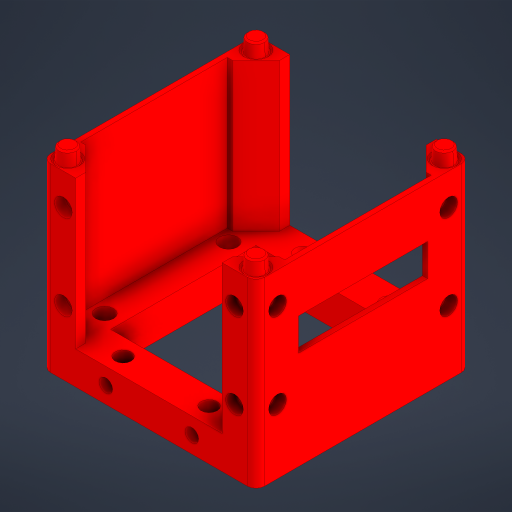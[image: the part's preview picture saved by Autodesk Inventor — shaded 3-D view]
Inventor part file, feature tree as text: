
AUTODESK INVENTOR PART (.ipt)
format: ipt  version: 2023.3 (Build 273359000, 359)  size: 446,976 bytes
history: native  units: mm
features: extrude x9, chamfer x7, sketch x5, projected_geometry x2, pattern_linear x1, pattern_circular x1, fillet x1
ambient origin geometry x8: Origin, YZ Plane, XZ Plane, XY Plane, X Axis, Y Axis, Z Axis, Center Point
bodies: Solid1 (feature_tree)
feature tree (26):
  sketch  "Sketch1"  dims[d0=49.8mm d1=49.8mm]
  extrude  "Extrusion1"  Depth=49.8mm
  extrude  "Extrusion2"  Depth=8.0mm
  extrude  "Extrusion3"  Depth=4.1mm
  extrude  "Extrusion4"  Depth=3.0mm
  chamfer  "Chamfer1"  Distance=4.2625mm
  chamfer  "Chamfer2"  Distance=0.675mm
  chamfer  "Chamfer3"  Distance=7.85mm
  chamfer  "Chamfer4"  Distance=7.85mm
  chamfer  "Chamfer5"  Distance=5.5mm
  chamfer  "Chamfer6"  Distance=5.5mm
  sketch  "Sketch2"  dims[d2=8.0mm d3=10.5mm]
  extrude  "Extrusion5"  Depth=10.0mm TaperAngle=360.0deg
  extrude  "Extrusion6"  Depth=7.7mm TaperAngle=0.0deg
  pattern_linear  "Rectangular Pattern1"  Spacing1=34.4mm  [1 undecoded]
  pattern_circular  "Circular Pattern1"  [2 undecoded]
  extrude  "Extrusion7"  Depth=10.0mm TaperAngle=0.0deg
  fillet  "Fillet1"  Radius=2.0mm
  chamfer  "Chamfer7"  Distance=0.375mm Angle=45.0deg
  extrude  "Extrusion8"  Depth=2.0mm
  extrude  "Extrusion9"  Depth=2.0mm
  sketch  "Sketch3"  dims[d4=10.5mm d5=4.1mm]
  projected_geometry  "Projected Loop1"
  sketch  "Sketch4"  dims[d6=4.15mm d7=3.0mm]
  projected_geometry  "Projected Loop2"
  sketch  "Sketch5"  dims[d8=3.0mm d9=4.2625mm d10=0.675mm d11=7.85mm d12=7.85mm d13=5.5mm d14=5.5mm d15=40.0mm d17=360.0deg d19=7.7mm d20=0.0mm d21=34.4mm d22=0.0mm d23=0.375mm d24=0.0mm d25=3.25mm d26=0.0mm d27=0.5mm d28=2.0mm d29=45.0deg d30=0.375mm d31=2.0mm d32=45.0deg d33=2.75mm d34=2.0mm d35=0.436332mm d36=2.75mm d37=2.0mm d38=0.436332mm d39=2.75mm d40=2.0mm d41=0.436332mm d42=2.75mm d43=2.0mm d44=0.436332mm d45=10.0mm d46=3.125mm d47=5.0mm d48=15.0mm d49=4.125mm d50=3.25mm d51=0.0mm d52=2.5mm d53=0.0mm d54=20.0mm d56=19.8mm d57=40.0mm d58=360.0deg d60=3.75mm d61=5.0mm d62=5.0mm d63=5.4125mm d64=0.0mm d65=2.0mm d66=0.025mm d67=2.0mm d68=0.436332mm d69=10.0mm d70=0.0mm d71=26.625mm d72=30.0mm d73=7.5mm d74=10.0mm d75=0.0mm]
note: 3 required parameter values undecoded (feature->parameter linkage not recoverable at this tier; creation-order binding heuristic only, values carry confidence <= 0.55)
